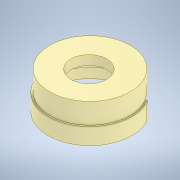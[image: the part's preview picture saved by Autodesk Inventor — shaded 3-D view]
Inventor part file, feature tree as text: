
AUTODESK INVENTOR PART (.ipt)
format: ipt  version: 2022 (Build 260153000, 153)  size: 192,512 bytes
history: native  units: mm
features: extrude x5, sketch x4, revolve x1
ambient origin geometry x8: Origin, YZ Plane, XZ Plane, XY Plane, X Axis, Y Axis, Z Axis, Center Point
bodies: Solid1 (feature_tree)
feature tree (10):
  revolve  "Revolution1"  [1 undecoded]
  sketch  "Sketch5"  dims[d2=16.2mm d3=2.0mm]
  extrude  "Extrusion2"  Depth=2.0mm
  extrude  "Extrusion3"  Depth=1.5mm
  extrude  "Extrusion5"  Depth=18.0mm
  extrude  "Extrusion6"  TaperAngle=360.0deg  [1 undecoded]
  extrude  "Extrusion8"  Depth=18.0mm
  sketch  "Sketch1"  dims[d0=6.55mm d1=14.6mm]
  sketch  "Sketch7"  dims[d4=8.5mm d5=1.5mm]
  sketch  "Sketch8"  dims[d6=3.0mm d7=2.5mm d8=360.0deg d29=1.0mm d30=70.0mm d31=73.0mm d32=3.0mm d33=0.0mm d34=23.7mm d35=0.0mm d41=10.0mm d42=0.0mm d43=73.0mm d44=1.0mm d45=76.0mm d46=10.0mm d47=0.0mm d50=5.0mm d51=0.0mm d55=0.0mm d56=0.0mm d60=19.5mm d61=7.5mm d62=18.0mm]
note: 2 required parameter values undecoded (feature->parameter linkage not recoverable at this tier; creation-order binding heuristic only, values carry confidence <= 0.55)